# Revit family: Plumbing-Fix_Faucet_Stern_Foot-Washfree
name_source: partatom
category: Plumbing Fixtures
revit_build: Autodesk Revit 2015 (Build: 20140606_1530(x64)
units: mm (PartAtom-declared; Revit-internal decimal feet)

## types (3) — shared parameters
Assembly Code = D2010300
Available Options = as Specified
Body Construction = Brass
CW Connection = Yes
CWFU = 1
Default Elevation = 0' - 0"
Description = Stern Wall Mounted Foot Wash Faucet - Foot Washfree as Specified
HW Connection = Yes
HWFU = 1
Keynote = 22 40 00
Manufacturer = Stern Engineering
Manufacturer Website = http://www.sternfaucets.com
Model = Foot Washfree
Operating Pressure Range = 7.26 - 116 PSI  ;  0.5 - 8 bar
Operating Temperature Range = Up to 149 F / 65 C
Piping_Flow = 2 GPM
Piping_Inlet Diameter = 1"
Power Supply = 9V Transformer
Product Data = http://www.arcat.com
Product Features = Exposed Installation
Revision = R1_2018-04
Sales Information = http://www.sternfaucets.com
Standards Conformance = as Specified
Type Comments = as Specified
URL = http://www.sternfaucets.com
Unit Height = 0' - 0"
Unit Width = 0' - 2 1/4"
Vent Connection = No
Warranty Duration (Years) = 2
Waste Connection = No
zero-valued in all types: Cost, Expected Lifespan (Years), Maintenance Schedule (Months), WFU

## type names (no varying parameters)
- 2.38 GPM
- 1.85 GPM
- 1.59 GPM

## geometry (parser evidence)
native form markers: Sweep x2
no freeform markers — native parametric forms only
